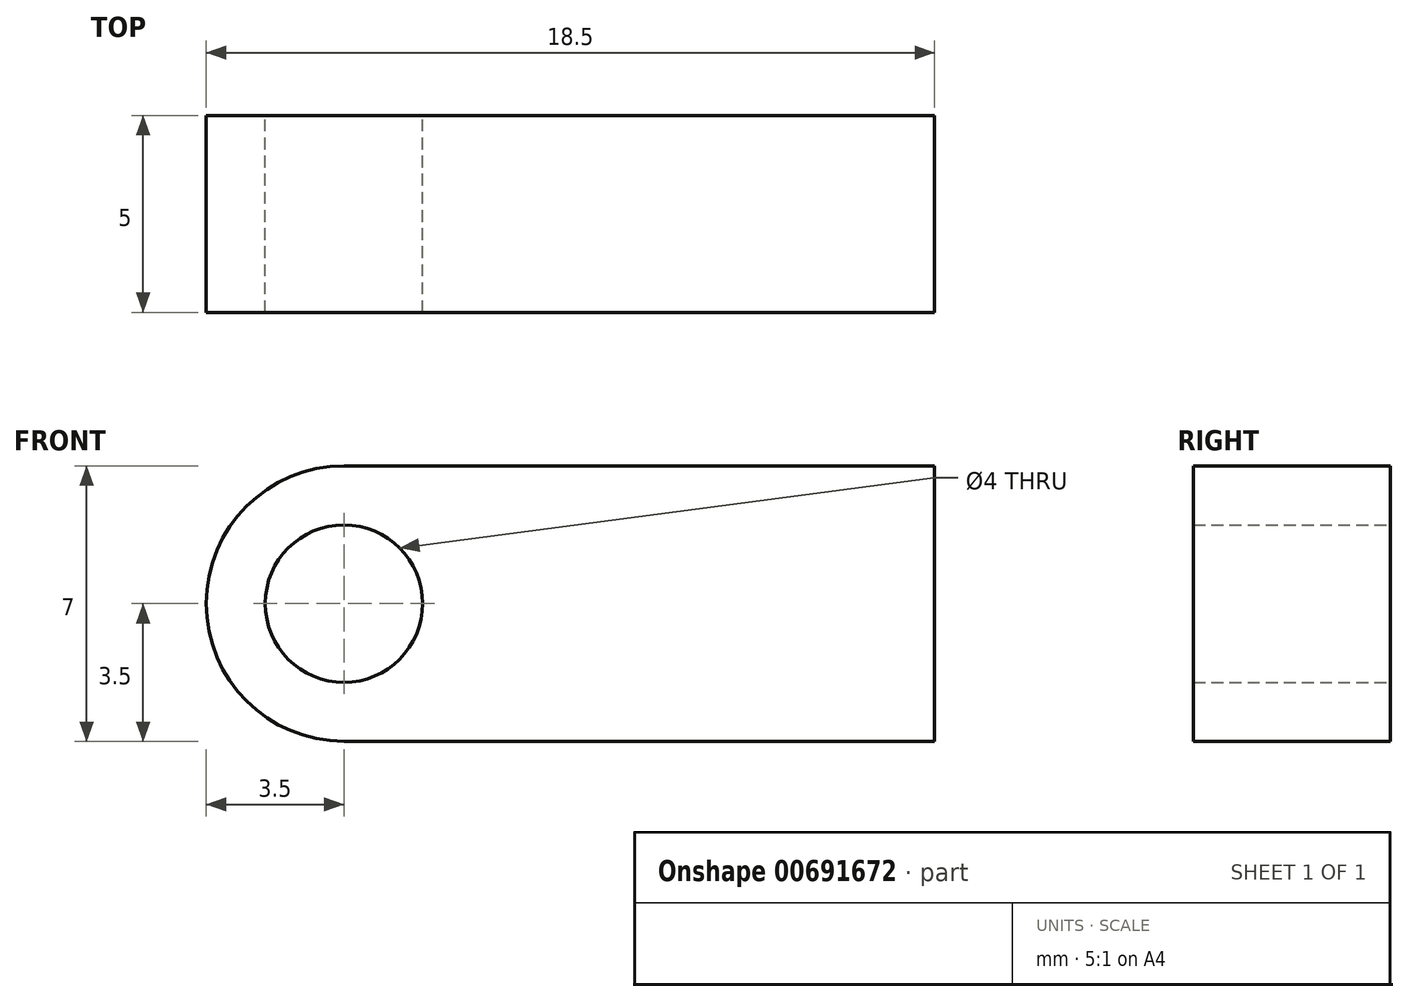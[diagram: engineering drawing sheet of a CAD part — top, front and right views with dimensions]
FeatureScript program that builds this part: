
annotation { "Feature Type Name" : "Feature", "Feature Type Description" : "" }
export const myFeature = defineFeature(function(context is Context, id is Id, definition is map)
    precondition{}
    {
        {
            var Q0;
            Q0=qCreatedBy(makeId("Front.planeOp"),FACE);
            var sketch = newSketch(context, id + "F0", { "sketchPlane" : qUnion([Q0])});
            skLineSegment(sketch, "E0.bottom", {"start": v(-7.5, 3.5) * mm, "end": v(7.5, 3.5) * mm});
            skLineSegment(sketch, "E0.top", {"start": v(-7.5, -3.5) * mm, "end": v(7.5, -3.5) * mm});
            skLineSegment(sketch, "E0.left", {"start": v(-7.5, 3.5) * mm, "end": v(-7.5, -3.5) * mm});
            skLineSegment(sketch, "E0.right", {"start": v(7.5, 3.5) * mm, "end": v(7.5, -3.5) * mm});
            skPoint(sketch, "E0.middle", {"position": v(0, 0) * mm});
            skCircle(sketch, "E1", {"center": v(-7.5, 0) * mm, "radius": 3.5 * mm});
            skCircle(sketch, "E2", {"center": v(-7.5, 0) * mm, "radius": 2 * mm});
            skSolve(sketch);
        }
        {
            var Q0;
            {var subQ1=sQuery(id+"F0.wireOp",EDGE,"E0.left");var subQ3=sQuery(id+"F0.wireOp",EDGE,"E2");var subQ4=makeQuery(id+"F0.imprint","INTERSECT",VERTEX,{"disambiguationData":[OD(0.0)],"derivedFrom":[subQ1,subQ3]});Q0=makeQuery(id+"F0.imprint","IMPRINT",FACE,{"disambiguationData":[TD([[makeQuery(id+"F0.imprint","IMPRINT",EDGE,{"disambiguationData":[TD([[subQ4,-1.0]])],"derivedFrom":subQ3}),-1.0]])]});}
            var Q1;
            {var subQ1=sQuery(id+"F0.wireOp",EDGE,"E0.left");var subQ3=sQuery(id+"F0.wireOp",EDGE,"E2");var subQ4=makeQuery(id+"F0.imprint","INTERSECT",VERTEX,{"disambiguationData":[OD(0.0)],"derivedFrom":[subQ1,subQ3]});Q1=makeQuery(id+"F0.imprint","IMPRINT",FACE,{"disambiguationData":[TD([[makeQuery(id+"F0.imprint","IMPRINT",EDGE,{"disambiguationData":[TD([[subQ4,1.0]])],"derivedFrom":subQ3}),-1.0]])]});}
            var Q2;
            {var subQ0=sQuery(id+"F0.wireOp",EDGE,"E0.bottom");Q2=makeQuery(id+"F0.imprint","IMPRINT",FACE,{"disambiguationData":[TD([[makeQuery(id+"F0.imprint","IMPRINT",EDGE,{"derivedFrom":subQ0}),-1.0]])]});}
            extrude(context, id + "F1", {"entities" : qUnion([Q0, Q1, Q2]), "depth" : 5 * mm, "offsetDistance" : 25 * mm});
        }
    });
